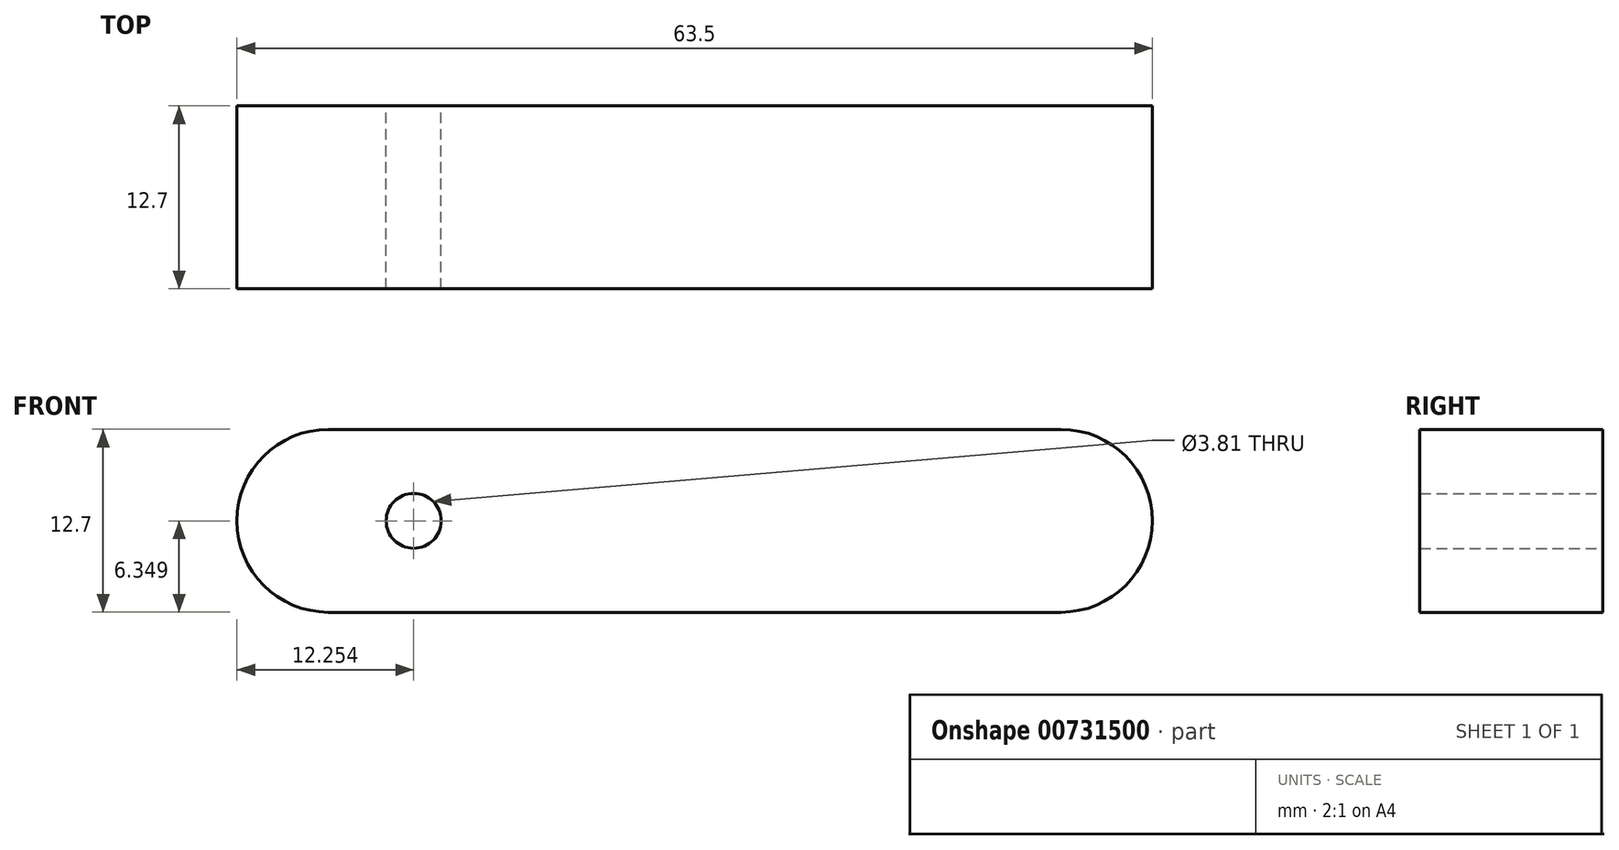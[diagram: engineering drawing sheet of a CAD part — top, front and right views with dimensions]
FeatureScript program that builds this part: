
annotation { "Feature Type Name" : "Feature", "Feature Type Description" : "" }
export const myFeature = defineFeature(function(context is Context, id is Id, definition is map)
    precondition{}
    {
        {
            var Q0;
            Q0=qCreatedBy(makeId("Front.planeOp"),FACE);
            var sketch = newSketch(context, id + "F0", { "sketchPlane" : qUnion([Q0])});
            skLineSegment(sketch, "E0.bottom", {"start": v(-32.81, 3.4) * mm, "end": v(17.99, 3.4) * mm});
            skLineSegment(sketch, "E0.top", {"start": v(-32.81, -9.3) * mm, "end": v(17.99, -9.3) * mm});
            skLineSegment(sketch, "E0.left", {"start": v(-32.81, 3.4) * mm, "end": v(-32.81, -9.3) * mm});
            skLineSegment(sketch, "E0.right", {"start": v(17.99, 3.4) * mm, "end": v(17.99, -9.3) * mm});
            skArc(sketch, "E1", {"start": v(-32.81, 3.4) * mm, "mid": v(-39.16, -2.95) * mm, "end": v(-32.81, -9.3) * mm});
            skArc(sketch, "E2", {"start": v(17.99, -9.3) * mm, "mid": v(24.34, -2.95) * mm, "end": v(17.99, 3.4) * mm});
            skCircle(sketch, "E3", {"center": v(-26.9, -2.95) * mm, "radius": 1.9 * mm});
            skSolve(sketch);
        }
        {
            var Q0;
            Q0 = qSketchRegion(id + "F0", true);
            extrude(context, id + "F1", {"entities" : qUnion([Q0]), "depth" : 12.7 * mm, "offsetDistance" : 25.4 * mm});
        }
    });
